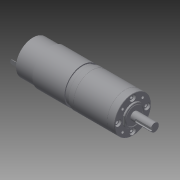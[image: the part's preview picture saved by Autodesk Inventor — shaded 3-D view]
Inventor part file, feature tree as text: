
AUTODESK INVENTOR PART (.ipt)
format: ipt  version: 2013 (Build 170138000, 138)  size: 288,256 bytes
history: native  units: in
note: dims shown in document units (in); Inventor stores cm internally (conversion verified against a paired STEP export)
features: mirror x1, other x1, imported_body x1
ambient origin geometry x8: Origin, YZ Plane, XZ Plane, XY Plane, X Axis, Y Axis, Z Axis, Center Point
feature tree (3):
  mirror  "Mirror2"
  other  "PG-711"
  imported_body  "Base1"
